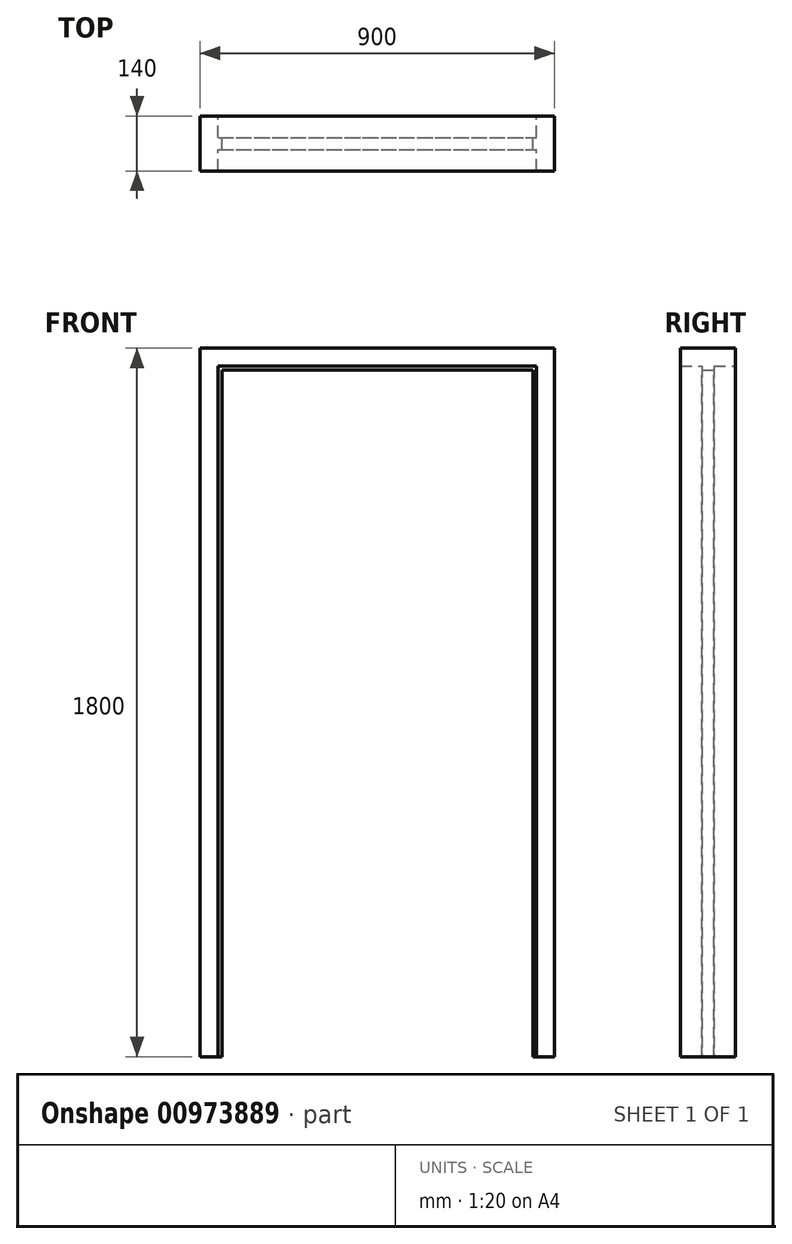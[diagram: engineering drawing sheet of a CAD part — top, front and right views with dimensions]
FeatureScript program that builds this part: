
annotation { "Feature Type Name" : "Feature", "Feature Type Description" : "" }
export const myFeature = defineFeature(function(context is Context, id is Id, definition is map)
    precondition{}
    {
        {
            var Q0;
            Q0=qCreatedBy(makeId("Front.planeOp"),FACE);
            var sketch = newSketch(context, id + "F0", { "sketchPlane" : qUnion([Q0])});
            skLineSegment(sketch, "E0.bottom", {"start": v(-450, 1800) * mm, "end": v(450, 1800) * mm});
            skLineSegment(sketch, "E0.top", {"start": v(-450, 0) * mm, "end": v(450, 0) * mm, "construction": true});
            skLineSegment(sketch, "E0.left", {"start": v(-450, 1800) * mm, "end": v(-450, 0) * mm});
            skLineSegment(sketch, "E0.right", {"start": v(450, 1800) * mm, "end": v(450, 0) * mm});
            skPoint(sketch, "E0.middle", {"position": v(0, 900) * mm});
            skLineSegment(sketch, "E1", {"start": v(0, 0) * mm, "end": v(0, 900) * mm, "construction": true});
            skLineSegment(sketch, "E2", {"start": v(-405, 0) * mm, "end": v(-450, 0) * mm});
            skLineSegment(sketch, "E3", {"start": v(-405, 0) * mm, "end": v(-405, 1755) * mm});
            skLineSegment(sketch, "E4", {"start": v(-405, 1755) * mm, "end": v(405, 1755) * mm});
            skLineSegment(sketch, "E5", {"start": v(405, 1755) * mm, "end": v(405, 0) * mm});
            skLineSegment(sketch, "E6", {"start": v(450, 0) * mm, "end": v(405, 0) * mm});
            skSolve(sketch);
        }
        {
            var Q0;
            Q0=makeQuery(id+"F0.imprint","IMPRINT",FACE,{"disambiguationData":[TD([[makeQuery(id+"F0.imprint","IMPRINT",EDGE,{"derivedFrom":sQuery(id+"F0.wireOp",EDGE,"E0.bottom")}),-1.0]])]});
            extrude(context, id + "F1", {"entities" : qUnion([Q0]), "endBound" : BoundingType.SYMMETRIC, "depth" : 140 * mm, "offsetDistance" : 25 * mm});
        }
        {
            var Q0;
            Q0=qCreatedBy(makeId("Front.planeOp"),FACE);
            var sketch = newSketch(context, id + "F2", { "sketchPlane" : qUnion([Q0])});
            skLineSegment(sketch, "E7.bottom", {"start": v(-405, 1755) * mm, "end": v(405, 1755) * mm});
            skLineSegment(sketch, "E7.top", {"start": v(-405, 0) * mm, "end": v(-395, 0) * mm});
            skLineSegment(sketch, "E7.left", {"start": v(-405, 1755) * mm, "end": v(-405, 0) * mm});
            skLineSegment(sketch, "E7.right", {"start": v(405, 1755) * mm, "end": v(405, 0) * mm});
            skLineSegment(sketch, "E8", {"start": v(-395, 0) * mm, "end": v(-395, 1745) * mm});
            skLineSegment(sketch, "E9", {"start": v(-395, 1745) * mm, "end": v(395, 1745) * mm});
            skLineSegment(sketch, "E10", {"start": v(395, 1745) * mm, "end": v(395, 0) * mm});
            skLineSegment(sketch, "E11.trimOffspring", {"start": v(395, 0) * mm, "end": v(405, 0) * mm});
            skSolve(sketch);
        }
        {
            var Q0;
            Q0 = qSketchRegion(id + "F2", true);
            extrude(context, id + "F3", {"entities" : qUnion([Q0]), "operationType" : NewBodyOperationType.ADD, "endBound" : BoundingType.SYMMETRIC, "depth" : 30 * mm, "offsetDistance" : 25 * mm});
        }
    });
